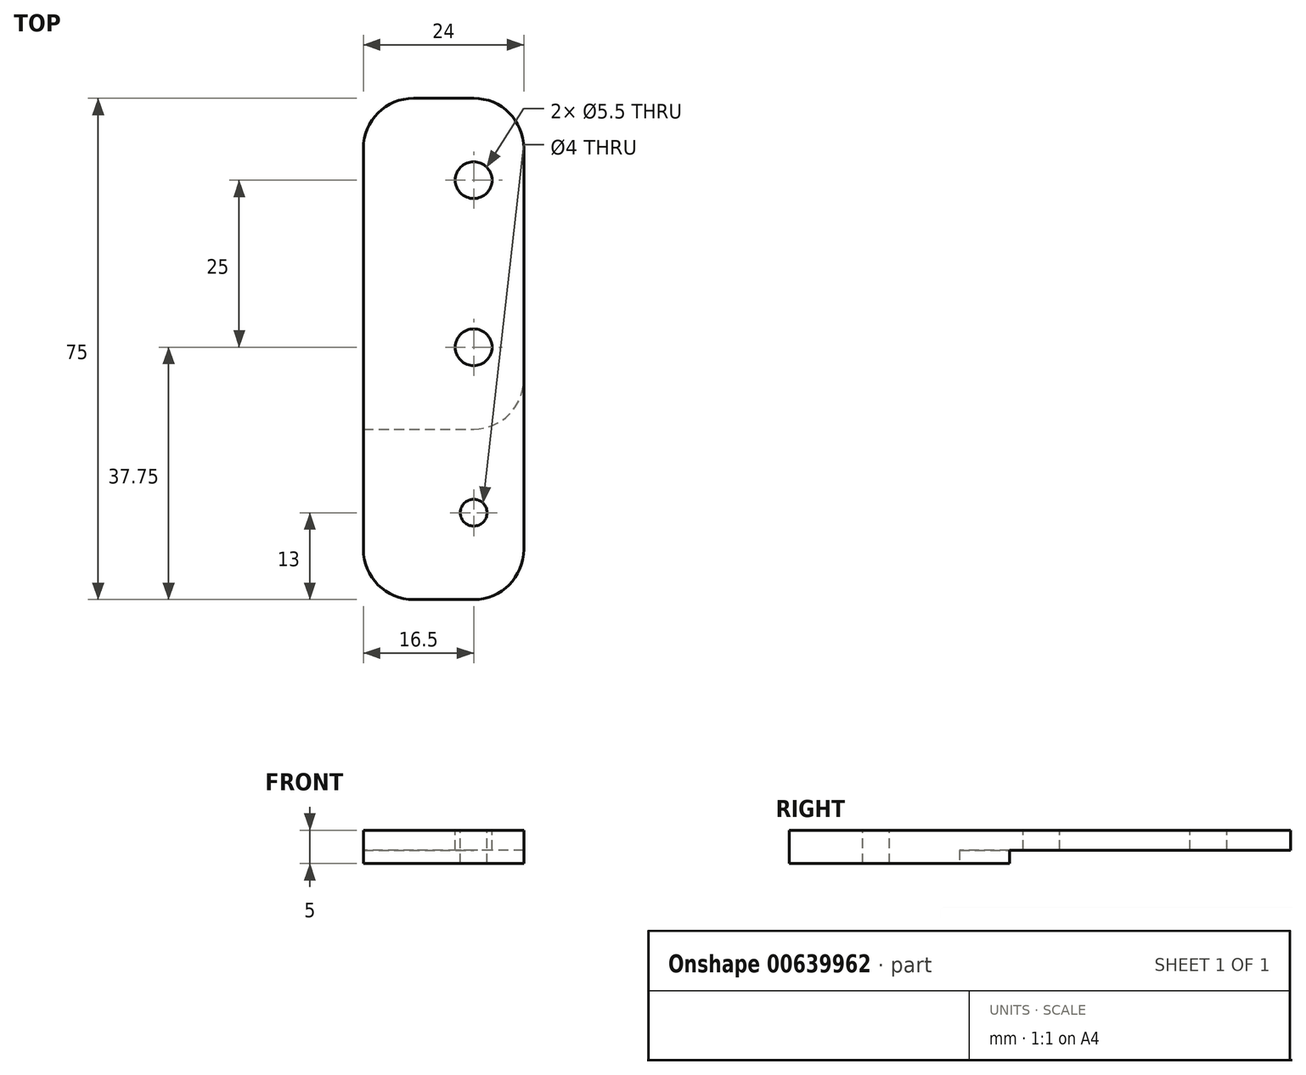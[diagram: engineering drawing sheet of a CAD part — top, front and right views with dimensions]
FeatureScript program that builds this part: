
annotation { "Feature Type Name" : "Feature", "Feature Type Description" : "" }
export const myFeature = defineFeature(function(context is Context, id is Id, definition is map)
    precondition{}
    {
        {
            var Q0;
            Q0=qCreatedBy(makeId("Top.planeOp"),FACE);
            var sketch = newSketch(context, id + "F0", { "sketchPlane" : qUnion([Q0])});
            skLineSegment(sketch, "E0.bottom", {"start": v(12, -37.5) * mm, "end": v(-12, -37.5) * mm});
            skLineSegment(sketch, "E0.top", {"start": v(12, 37.5) * mm, "end": v(-12, 37.5) * mm});
            skLineSegment(sketch, "E0.left", {"start": v(12, -37.5) * mm, "end": v(12, 37.5) * mm});
            skLineSegment(sketch, "E0.right", {"start": v(-12, -37.5) * mm, "end": v(-12, 37.5) * mm});
            skPoint(sketch, "E0.middle", {"position": v(0, 0) * mm});
            skSolve(sketch);
        }
        {
            var Q0;
            Q0=makeQuery(id+"F0.imprint","IMPRINT",FACE,{"disambiguationData":[TD([[makeQuery(id+"F0.imprint","IMPRINT",EDGE,{"derivedFrom":sQuery(id+"F0.wireOp",EDGE,"E0.bottom")}),-1.0]])]});
            extrude(context, id + "F1", {"entities" : qUnion([Q0]), "depth" : 5 * mm, "offsetDistance" : 25 * mm});
        }
        {
            var Q0;
            Q0=makeQuery(id+"F1.opExtrude","CAP_FACE",FACE,{"disambiguationData":[OSD([sQuery(id+"F0.wireOp",EDGE,"E0.bottom"),sQuery(id+"F0.wireOp",EDGE,"E0.top"),sQuery(id+"F0.wireOp",EDGE,"E0.left"),sQuery(id+"F0.wireOp",EDGE,"E0.right")])],"isStart":false});
            var sketch = newSketch(context, id + "F2", { "sketchPlane" : qUnion([Q0])});
            skCircle(sketch, "E1", {"center": v(4.5, 25.25) * mm, "radius": 2.75 * mm});
            skCircle(sketch, "E2", {"center": v(4.5, 0.25) * mm, "radius": 2.75 * mm});
            skCircle(sketch, "E3", {"center": v(4.5, -24.5) * mm, "radius": 2 * mm});
            skSolve(sketch);
        }
        {
            var Q0;
            Q0=makeQuery(id+"F2.imprint","IMPRINT",FACE,{"disambiguationData":[TD([[makeQuery(id+"F2.imprint","IMPRINT",EDGE,{"derivedFrom":sQuery(id+"F2.wireOp",EDGE,"E1")}),1.0]])]});
            var Q1;
            Q1=makeQuery(id+"F2.imprint","IMPRINT",FACE,{"disambiguationData":[TD([[makeQuery(id+"F2.imprint","IMPRINT",EDGE,{"derivedFrom":sQuery(id+"F2.wireOp",EDGE,"E2")}),1.0]])]});
            var Q2;
            Q2=makeQuery(id+"F2.imprint","IMPRINT",FACE,{"disambiguationData":[TD([[makeQuery(id+"F2.imprint","IMPRINT",EDGE,{"derivedFrom":sQuery(id+"F2.wireOp",EDGE,"E3")}),1.0]])]});
            extrude(context, id + "F3", {"entities" : qUnion([Q0, Q1, Q2]), "operationType" : NewBodyOperationType.REMOVE, "oppositeDirection" : true, "depth" : 5 * mm, "offsetDistance" : 25 * mm});
        }
        {
            var Q0;
            Q0=makeQuery(id+"F1.opExtrude","SWEPT_EDGE",EDGE,{"disambiguationData":[OSD([sQuery(id+"F0.wireOp",EDGE,"E0.top"),sQuery(id+"F0.wireOp",EDGE,"E0.left")])]});
            var Q1;
            Q1=makeQuery(id+"F1.opExtrude","SWEPT_EDGE",EDGE,{"disambiguationData":[OSD([sQuery(id+"F0.wireOp",EDGE,"E0.top"),sQuery(id+"F0.wireOp",EDGE,"E0.right")])]});
            var Q2;
            Q2=makeQuery(id+"F1.opExtrude","SWEPT_EDGE",EDGE,{"disambiguationData":[OSD([sQuery(id+"F0.wireOp",EDGE,"E0.bottom"),sQuery(id+"F0.wireOp",EDGE,"E0.left")])]});
            var Q3;
            Q3=makeQuery(id+"F1.opExtrude","SWEPT_EDGE",EDGE,{"disambiguationData":[OSD([sQuery(id+"F0.wireOp",EDGE,"E0.bottom"),sQuery(id+"F0.wireOp",EDGE,"E0.right")])]});
            fillet(context, id + "F4", {"entities" : qUnion([Q0, Q1, Q2, Q3]), "radius" : 7.5 * mm, "tangentPropagation" : true, "allowEdgeOverflow" : false});
        }
        {
            var Q0;
            Q0=makeQuery(id+"F1.opExtrude","CAP_FACE",FACE,{"disambiguationData":[OSD([sQuery(id+"F0.wireOp",EDGE,"E0.bottom"),sQuery(id+"F0.wireOp",EDGE,"E0.top"),sQuery(id+"F0.wireOp",EDGE,"E0.left"),sQuery(id+"F0.wireOp",EDGE,"E0.right")])],"isStart":true});
            var sketch = newSketch(context, id + "F5", { "sketchPlane" : qUnion([Q0])});
            skLineSegment(sketch, "E4.bottom", {"start": v(-12, 12) * mm, "end": v(4.5, 12) * mm});
            skLineSegment(sketch, "E4.top", {"start": v(-12, -37.5) * mm, "end": v(12, -37.5) * mm});
            skLineSegment(sketch, "E4.left", {"start": v(-12, 12) * mm, "end": v(-12, -37.5) * mm});
            skLineSegment(sketch, "E4.right", {"start": v(12, 4.5) * mm, "end": v(12, -37.5) * mm});
            skPoint(sketch, "E5.visualSharp", {"position": v(12, 12) * mm});
            skArc(sketch, "E5.filletArc", {"start": v(12, 4.5) * mm, "mid": v(9.8, 9.8) * mm, "end": v(4.5, 12) * mm});
            skSolve(sketch);
        }
        {
            var Q0;
            {var subQ6=sQuery(id+"F5.wireOp",EDGE,"E4.bottom");Q0=makeQuery(id+"F5.imprint","IMPRINT",FACE,{"disambiguationData":[TD([[makeQuery(id+"F5.imprint","IMPRINT",EDGE,{"derivedFrom":subQ6}),-1.0]])]});}
            extrude(context, id + "F6", {"entities" : qUnion([Q0]), "operationType" : NewBodyOperationType.REMOVE, "oppositeDirection" : true, "depth" : 2 * mm, "offsetDistance" : 25 * mm});
        }
    });
